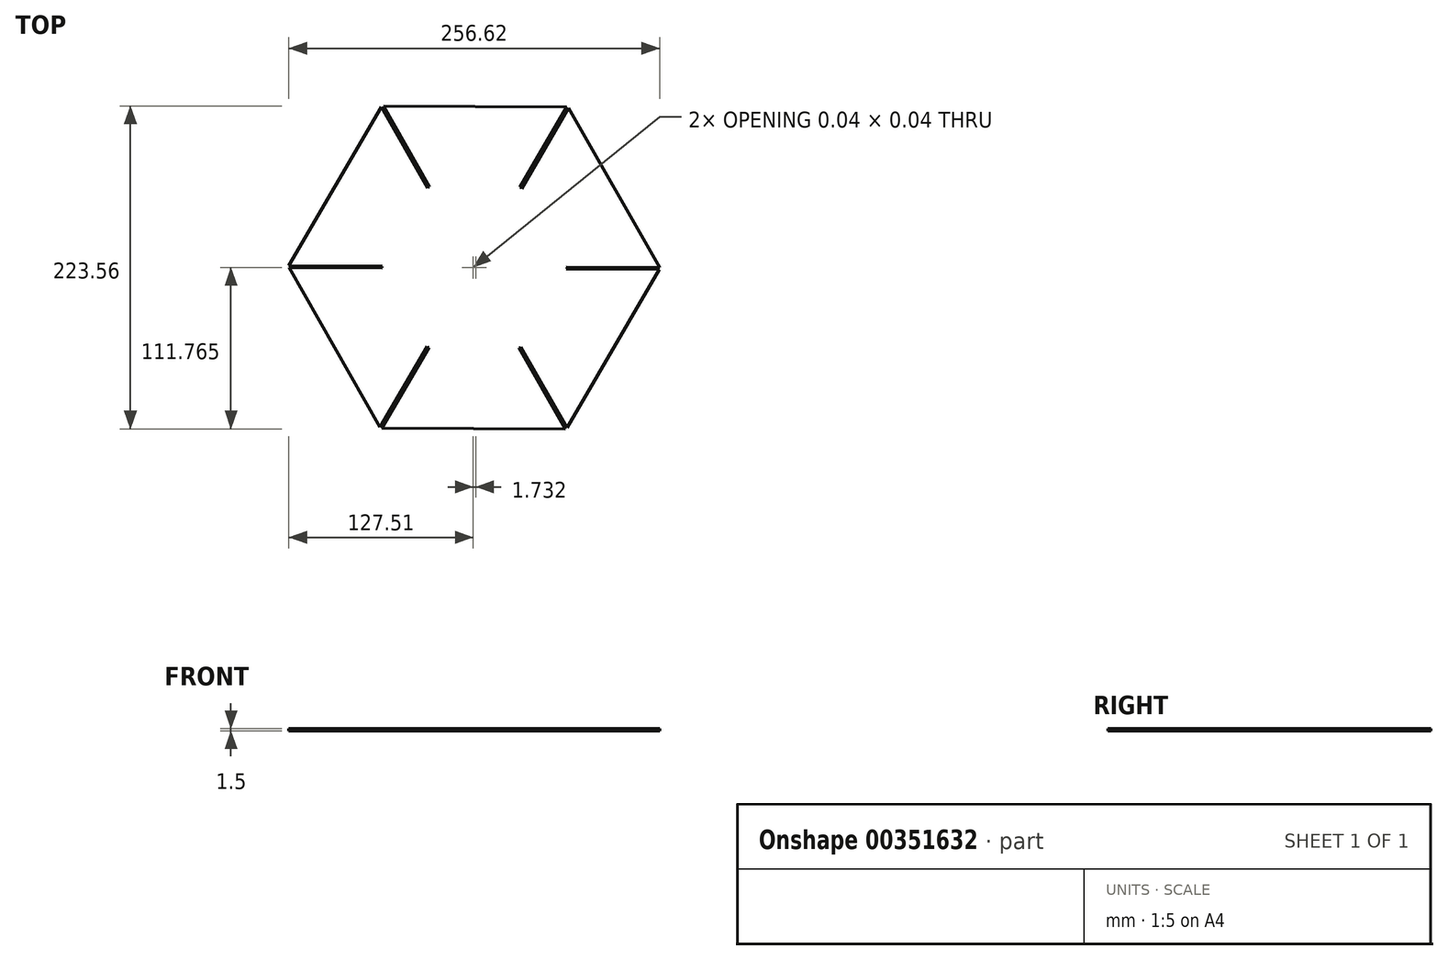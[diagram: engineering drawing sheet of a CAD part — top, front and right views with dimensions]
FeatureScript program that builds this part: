
annotation { "Feature Type Name" : "Feature", "Feature Type Description" : "" }
export const myFeature = defineFeature(function(context is Context, id is Id, definition is map)
    precondition{}
    {
        {
            var Q0;
            Q0=qCreatedBy(makeId("Top.planeOp"),FACE);
            var sketch = newSketch(context, id + "F0", { "sketchPlane" : qUnion([Q0])});
            skLineSegment(sketch, "E0", {"start": v(-155.7, -56.32) * mm, "end": v(-154.79, -56.32) * mm});
            skLineSegment(sketch, "E1", {"start": v(-91.56, -56.64) * mm, "end": v(-91.1, -57.46) * mm});
            skLineSegment(sketch, "E2", {"start": v(-59.78, -112.34) * mm, "end": v(-60.26, -113.16) * mm});
            skLineSegment(sketch, "E3", {"start": v(-92.13, -167.72) * mm, "end": v(-92.95, -167.72) * mm});
            skLineSegment(sketch, "E4", {"start": v(-156.26, -167.4) * mm, "end": v(-156.64, -166.74) * mm});
            skLineSegment(sketch, "E5", {"start": v(-188.05, -111.7) * mm, "end": v(-187.65, -111.01) * mm});
            skLineSegment(sketch, "E6", {"start": v(-204.44, 297.6) * mm, "end": v(-205.39, 297.15) * mm});
            skLineSegment(sketch, "E7", {"start": v(-46.33, 6.6) * mm, "end": v(-45.37, 7.07) * mm});
            skLineSegment(sketch, "E8", {"start": v(-289.5, 155.34) * mm, "end": v(-210.67, 293.96) * mm});
            skLineSegment(sketch, "E9", {"start": v(-289.2, 149.17) * mm, "end": v(-211.12, 10.13) * mm});
            skLineSegment(sketch, "E10", {"start": v(-205.5, 7.45) * mm, "end": v(-46.33, 7.45) * mm});
            skLineSegment(sketch, "E11", {"start": v(-40.08, 10.25) * mm, "end": v(38.74, 148.88) * mm});
            skLineSegment(sketch, "E12", {"start": v(-205.39, 297.15) * mm, "end": v(-45.26, 297.15) * mm});
            skLineSegment(sketch, "E13", {"start": v(-39.63, 294.08) * mm, "end": v(38.44, 155.05) * mm});
            skLineSegment(sketch, "E14", {"start": v(-289.5, 155.34) * mm, "end": v(38.44, 155.04) * mm});
            skLineSegment(sketch, "E15", {"start": v(38.74, 148.88) * mm, "end": v(-289.2, 149.17) * mm});
            skLineSegment(sketch, "E16", {"start": v(-211.12, 10.13) * mm, "end": v(-45.26, 296.76) * mm});
            skLineSegment(sketch, "E17", {"start": v(-39.63, 294.08) * mm, "end": v(-205.5, 7.45) * mm});
            skLineSegment(sketch, "E18", {"start": v(-46.33, 7.45) * mm, "end": v(-210.67, 293.96) * mm});
            skLineSegment(sketch, "E19", {"start": v(-204.44, 297.6) * mm, "end": v(-40.08, 10.25) * mm});
            skLineSegment(sketch, "E20", {"start": v(289.2, -185.96) * mm, "end": v(289.2, -191.82) * mm});
            skLineSegment(sketch, "E21", {"start": v(102.93, -77.52) * mm, "end": v(224.18, -77.52) * mm});
            skLineSegment(sketch, "E22", {"start": v(229.77, -80.58) * mm, "end": v(289.2, -185.96) * mm});
            skLineSegment(sketch, "E23", {"start": v(289.49, -192.12) * mm, "end": v(229.37, -297.09) * mm});
            skLineSegment(sketch, "E24", {"start": v(102.83, -299.86) * mm, "end": v(224.07, -299.86) * mm});
            skLineSegment(sketch, "E25", {"start": v(37.8, -191.82) * mm, "end": v(97.24, -297.2) * mm});
            skLineSegment(sketch, "E26", {"start": v(37.52, -185.65) * mm, "end": v(97.64, -80.7) * mm});
            skLineSegment(sketch, "E27", {"start": v(97.64, -80.7) * mm, "end": v(224.07, -300.25) * mm});
            skLineSegment(sketch, "E28", {"start": v(229.37, -297.1) * mm, "end": v(102.93, -77.52) * mm});
            skLineSegment(sketch, "E29", {"start": v(224.18, -77.92) * mm, "end": v(97.23, -297.2) * mm});
            skLineSegment(sketch, "E30", {"start": v(102.83, -299.86) * mm, "end": v(229.77, -80.58) * mm});
            skLineSegment(sketch, "E31", {"start": v(289.2, -185.96) * mm, "end": v(37.52, -185.65) * mm});
            skLineSegment(sketch, "E32", {"start": v(38.74, -191.82) * mm, "end": v(289.2, -191.82) * mm});
            skLineSegment(sketch, "E33", {"start": v(104.3, 19.99) * mm, "end": v(104.01, 19.69) * mm});
            skLineSegment(sketch, "E34", {"start": v(199.71, -14.35) * mm, "end": v(140.43, 88.3) * mm});
            skLineSegment(sketch, "E35", {"start": v(145.63, 91.64) * mm, "end": v(204.8, -11.43) * mm});
            skLineSegment(sketch, "E36", {"start": v(199.71, 60.2) * mm, "end": v(217.63, 91.25) * mm});
            skLineSegment(sketch, "E37", {"start": v(223.14, 88.44) * mm, "end": v(204.8, 57.27) * mm});
            skLineSegment(sketch, "E38", {"start": v(204.8, -11.43) * mm, "end": v(222.71, -42.47) * mm});
            skLineSegment(sketch, "E39", {"start": v(217.52, -45.8) * mm, "end": v(199.71, -14.35) * mm});
            skLineSegment(sketch, "E40", {"start": v(204.8, 57.27) * mm, "end": v(181.58, 17.05) * mm});
            skLineSegment(sketch, "E41", {"start": v(181.58, 17.05) * mm, "end": v(145.52, -45.42) * mm});
            skLineSegment(sketch, "E42", {"start": v(140.02, -42.6) * mm, "end": v(178.12, 23.03) * mm});
            skLineSegment(sketch, "E43", {"start": v(178.12, 23.03) * mm, "end": v(179.76, 25.85) * mm});
            skLineSegment(sketch, "E44", {"start": v(179.76, 25.85) * mm, "end": v(181.6, 29) * mm});
            skLineSegment(sketch, "E45", {"start": v(181.6, 29) * mm, "end": v(199.71, 60.2) * mm});
            skLineSegment(sketch, "E46", {"start": v(104.02, 26.15) * mm, "end": v(140.43, 88.3) * mm});
            skLineSegment(sketch, "E47", {"start": v(217.63, 91.25) * mm, "end": v(145.63, 91.64) * mm});
            skLineSegment(sketch, "E48", {"start": v(223.14, 88.44) * mm, "end": v(258.85, 25.85) * mm});
            skLineSegment(sketch, "E49", {"start": v(259.13, 19.69) * mm, "end": v(222.72, -42.46) * mm});
            skLineSegment(sketch, "E50", {"start": v(217.52, -45.8) * mm, "end": v(145.52, -45.42) * mm});
            skLineSegment(sketch, "E51", {"start": v(140.02, -42.6) * mm, "end": v(104.01, 19.69) * mm});
            skLineSegment(sketch, "E52", {"start": v(104.3, 19.99) * mm, "end": v(259.13, 19.99) * mm});
            skLineSegment(sketch, "E53", {"start": v(104.02, 26.15) * mm, "end": v(258.85, 26.15) * mm});
            skLineSegment(sketch, "E54", {"start": v(134.38, 175.06) * mm, "end": v(170.48, 174.76) * mm});
            skLineSegment(sketch, "E55", {"start": v(170.48, 174.76) * mm, "end": v(170.48, 168.9) * mm});
            skLineSegment(sketch, "E56", {"start": v(170.48, 168.9) * mm, "end": v(134.66, 168.9) * mm});
            skLineSegment(sketch, "E57", {"start": v(134.66, 168.9) * mm, "end": v(134.37, 168.6) * mm});
            skLineSegment(sketch, "E58", {"start": v(176, 240.55) * mm, "end": v(193.8, 209.12) * mm});
            skLineSegment(sketch, "E59", {"start": v(193.8, 209.12) * mm, "end": v(188.72, 206.17) * mm});
            skLineSegment(sketch, "E60", {"start": v(253.49, 237.35) * mm, "end": v(235.16, 206.19) * mm});
            skLineSegment(sketch, "E61", {"start": v(235.16, 206.19) * mm, "end": v(230.07, 209.12) * mm});
            skLineSegment(sketch, "E62", {"start": v(289.5, 168.6) * mm, "end": v(253.4, 168.9) * mm});
            skLineSegment(sketch, "E63", {"start": v(253.4, 168.9) * mm, "end": v(253.4, 174.76) * mm});
            skLineSegment(sketch, "E64", {"start": v(247.87, 103.11) * mm, "end": v(230.07, 134.56) * mm});
            skLineSegment(sketch, "E65", {"start": v(230.07, 134.56) * mm, "end": v(235.15, 137.49) * mm});
            skLineSegment(sketch, "E66", {"start": v(170.37, 106.32) * mm, "end": v(188.71, 137.49) * mm});
            skLineSegment(sketch, "E67", {"start": v(188.71, 137.49) * mm, "end": v(193.8, 134.54) * mm});
            skLineSegment(sketch, "E68", {"start": v(134.38, 175.06) * mm, "end": v(170.8, 237.2) * mm});
            skLineSegment(sketch, "E69", {"start": v(248, 240.16) * mm, "end": v(176, 240.55) * mm});
            skLineSegment(sketch, "E70", {"start": v(253.49, 237.35) * mm, "end": v(289.2, 174.76) * mm});
            skLineSegment(sketch, "E71", {"start": v(289.5, 168.6) * mm, "end": v(253.08, 106.45) * mm});
            skLineSegment(sketch, "E72", {"start": v(247.87, 103.11) * mm, "end": v(175.87, 103.5) * mm});
            skLineSegment(sketch, "E73", {"start": v(170.37, 106.32) * mm, "end": v(134.37, 168.6) * mm});
            skLineSegment(sketch, "E74", {"start": v(4.67, 234.76) * mm, "end": v(40.77, 234.46) * mm});
            skLineSegment(sketch, "E75", {"start": v(40.77, 234.46) * mm, "end": v(40.77, 228.6) * mm});
            skLineSegment(sketch, "E76", {"start": v(40.77, 228.6) * mm, "end": v(4.96, 228.6) * mm});
            skLineSegment(sketch, "E77", {"start": v(4.96, 228.6) * mm, "end": v(4.66, 228.3) * mm});
            skLineSegment(sketch, "E78", {"start": v(46.28, 300.25) * mm, "end": v(64.09, 268.81) * mm});
            skLineSegment(sketch, "E79", {"start": v(64.09, 268.81) * mm, "end": v(59.01, 265.88) * mm});
            skLineSegment(sketch, "E80", {"start": v(123.78, 297.05) * mm, "end": v(105.45, 265.88) * mm});
            skLineSegment(sketch, "E81", {"start": v(105.45, 265.88) * mm, "end": v(100.36, 268.81) * mm});
            skLineSegment(sketch, "E82", {"start": v(123.78, 232.16) * mm, "end": v(123.78, 233.6) * mm});
            skLineSegment(sketch, "E83", {"start": v(118.17, 162.82) * mm, "end": v(100.36, 194.25) * mm});
            skLineSegment(sketch, "E84", {"start": v(100.36, 194.25) * mm, "end": v(105.45, 197.18) * mm});
            skLineSegment(sketch, "E85", {"start": v(40.67, 166.01) * mm, "end": v(59, 197.18) * mm});
            skLineSegment(sketch, "E86", {"start": v(59, 197.18) * mm, "end": v(64.09, 194.24) * mm});
            skLineSegment(sketch, "E87", {"start": v(4.67, 234.76) * mm, "end": v(41.09, 296.9) * mm});
            skLineSegment(sketch, "E88", {"start": v(118.28, 299.86) * mm, "end": v(46.28, 300.25) * mm});
            skLineSegment(sketch, "E89", {"start": v(123.78, 297.05) * mm, "end": v(159.79, 233.38) * mm});
            skLineSegment(sketch, "E90", {"start": v(159.79, 228.3) * mm, "end": v(123.37, 166.15) * mm});
            skLineSegment(sketch, "E91", {"start": v(118.17, 162.82) * mm, "end": v(46.17, 163.2) * mm});
            skLineSegment(sketch, "E92", {"start": v(40.67, 166.01) * mm, "end": v(4.66, 228.3) * mm});
            skLineSegment(sketch, "E93", {"start": v(4.67, 234.76) * mm, "end": v(40.77, 234.44) * mm});
            skLineSegment(sketch, "E94", {"start": v(-187.19, 0.06) * mm, "end": v(-188.48, -0.7) * mm});
            skLineSegment(sketch, "E95", {"start": v(-155.01, -55.91) * mm, "end": v(-156.3, -56.67) * mm});
            skLineSegment(sketch, "E96", {"start": v(-90.78, -57.24) * mm, "end": v(-92.08, -56.5) * mm});
            skLineSegment(sketch, "E97", {"start": v(-59, -0.89) * mm, "end": v(4.4, -111.99) * mm});
            skLineSegment(sketch, "E98", {"start": v(4.31, -113.49) * mm, "end": v(-60.13, -223.8) * mm});
            skLineSegment(sketch, "E99", {"start": v(-60.13, -223.8) * mm, "end": v(-188.83, -223.15) * mm});
            skLineSegment(sketch, "E100", {"start": v(-188.83, -223.15) * mm, "end": v(-253, -110.68) * mm});
            skLineSegment(sketch, "E101", {"start": v(-252.61, -111.37) * mm, "end": v(-187.7, -0.24) * mm});
            skLineSegment(sketch, "E102", {"start": v(-187.7, -0.24) * mm, "end": v(-59, -0.89) * mm});
            skLineSegment(sketch, "E103", {"start": v(-188.16, -0.86) * mm, "end": v(-156.11, -57.02) * mm});
            skLineSegment(sketch, "E104", {"start": v(-58.54, -1.7) * mm, "end": v(-91.1, -57.46) * mm});
            skLineSegment(sketch, "E105", {"start": v(-59.63, -112.34) * mm, "end": v(-59.78, -112.34) * mm});
            skLineSegment(sketch, "E106.0", {"start": v(-186.86, -0.12) * mm, "end": v(-154.79, -56.32) * mm});
            skLineSegment(sketch, "E107.0", {"start": v(-59.8, -0.88) * mm, "end": v(-92.35, -56.64) * mm});
            skPoint(sketch, "E108", {"position": v(-155.29, -167.4) * mm});
            skLineSegment(sketch, "E109.trimOffspring", {"start": v(-155.29, -167.4) * mm, "end": v(-187.84, -223.16) * mm});
            skLineSegment(sketch, "E110.trimOffspring", {"start": v(-122.96, -112.02) * mm, "end": v(-122.98, -112.06) * mm});
            skLineSegment(sketch, "E111.trimOffspring", {"start": v(-124.69, -112.02) * mm, "end": v(-124.71, -112.05) * mm});
            skLineSegment(sketch, "E112.trimOffspring", {"start": v(-123, -112.02) * mm, "end": v(-122.98, -112.06) * mm});
            skLineSegment(sketch, "E113.trimOffspring", {"start": v(-124.73, -112.02) * mm, "end": v(-124.71, -112.05) * mm});
            skLineSegment(sketch, "E114.trimOffspring", {"start": v(-92.95, -167.72) * mm, "end": v(-60.59, -224.43) * mm});
            skLineSegment(sketch, "E115.trimOffspring", {"start": v(-91.67, -166.94) * mm, "end": v(-59.28, -223.69) * mm});
            skLineSegment(sketch, "E116.trimOffspring", {"start": v(-156.64, -166.74) * mm, "end": v(-189.2, -222.5) * mm});
            skLineSegment(sketch, "E117.trimOffspring", {"start": v(-124.69, -112.02) * mm, "end": v(-124.73, -112.02) * mm});
            skLineSegment(sketch, "E118.trimOffspring", {"start": v(-122.96, -112.02) * mm, "end": v(-123, -112.02) * mm});
            skLineSegment(sketch, "E119", {"start": v(4.4, -111.99) * mm, "end": v(-60.17, -111.66) * mm});
            skLineSegment(sketch, "E120.0", {"start": v(4.31, -113.49) * mm, "end": v(-60.26, -113.16) * mm});
            skLineSegment(sketch, "E121.trimOffspring", {"start": v(-187.58, -112.52) * mm, "end": v(-253.1, -112.18) * mm});
            skLineSegment(sketch, "E122.trimOffspring", {"start": v(-187.65, -111.01) * mm, "end": v(-253, -110.68) * mm});
            skLineSegment(sketch, "E123.trimOffspring", {"start": v(-60.17, -111.66) * mm, "end": v(-59.78, -112.34) * mm});
            skLineSegment(sketch, "E124.trimOffspring", {"start": v(-91.67, -166.94) * mm, "end": v(-92.13, -167.72) * mm});
            skLineSegment(sketch, "E125.trimOffspring", {"start": v(-155.29, -167.4) * mm, "end": v(-156.26, -167.4) * mm});
            skLineSegment(sketch, "E126.trimOffspring", {"start": v(-187.58, -112.52) * mm, "end": v(-188.05, -111.7) * mm});
            skLineSegment(sketch, "E127.trimOffspring", {"start": v(-156.11, -57.02) * mm, "end": v(-155.7, -56.32) * mm});
            skLineSegment(sketch, "E128.trimOffspring", {"start": v(-92.35, -56.64) * mm, "end": v(-91.56, -56.64) * mm});
            skSolve(sketch);
        }
        {
            var Q0;
            {var subQ3=sQuery(id+"F0.wireOp",EDGE,"E0");Q0=makeQuery(id+"F0.imprint","IMPRINT",FACE,{"disambiguationData":[TD([[makeQuery(id+"F0.imprint","IMPRINT",EDGE,{"derivedFrom":subQ3}),-1.0]])]});}
            extrude(context, id + "F1", {"entities" : qUnion([Q0]), "depth" : 1.5 * mm});
        }
    });
